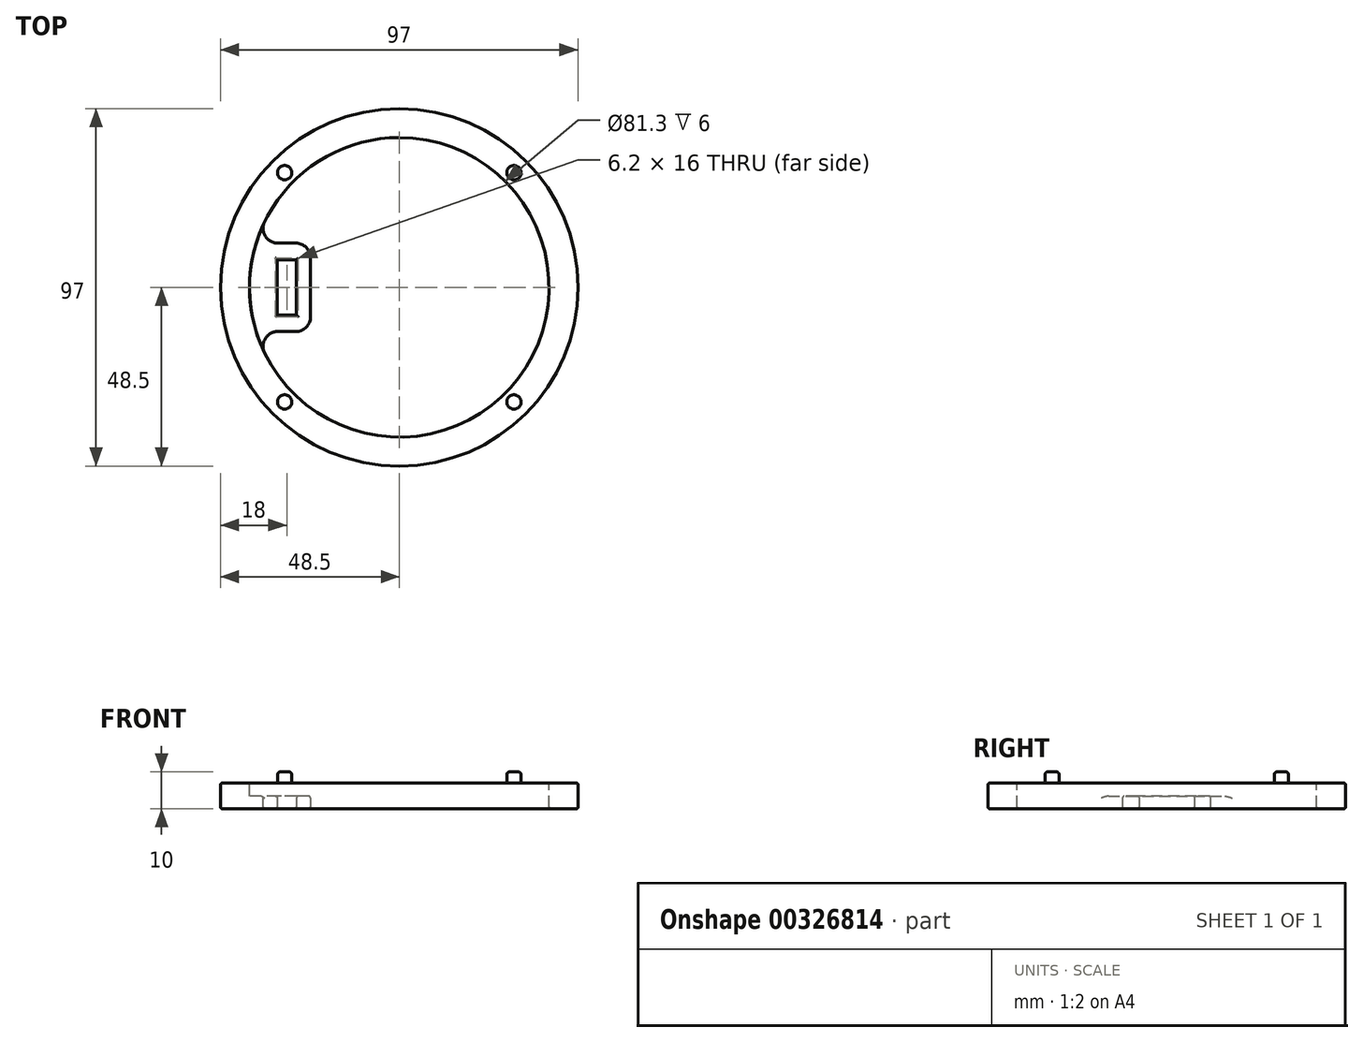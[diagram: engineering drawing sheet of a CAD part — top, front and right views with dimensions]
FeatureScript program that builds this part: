
annotation { "Feature Type Name" : "Feature", "Feature Type Description" : "" }
export const myFeature = defineFeature(function(context is Context, id is Id, definition is map)
    precondition{}
    {
        {
            var Q0;
            Q0=qCreatedBy(makeId("Top.planeOp"),FACE);
            var sketch = newSketch(context, id + "F0", { "sketchPlane" : qUnion([Q0])});
            skCircle(sketch, "E0", {"center": v(0, 0) * mm, "radius": 40.65 * mm});
            skCircle(sketch, "E1", {"center": v(0, 0) * mm, "radius": 48.5 * mm});
            skCircle(sketch, "E2", {"center": v(0, 0) * mm, "radius": 44 * mm, "construction": true});
            skCircle(sketch, "E3", {"center": v(-31.11, 31.11) * mm, "radius": 1.95 * mm});
            skCircle(sketch, "E4", {"center": v(31.11, -31.11) * mm, "radius": 1.95 * mm});
            skCircle(sketch, "E5", {"center": v(31.11, 31.11) * mm, "radius": 1.95 * mm});
            skCircle(sketch, "E6", {"center": v(-31.11, -31.11) * mm, "radius": 1.95 * mm});
            skLineSegment(sketch, "E7.0", {"start": v(-31.11, -31.11) * mm, "end": v(31.11, 31.11) * mm, "construction": true});
            skLineSegment(sketch, "E8.0", {"start": v(31.11, -31.11) * mm, "end": v(-31.11, 31.11) * mm, "construction": true});
            skSolve(sketch);
        }
        {
            var Q0;
            Q0=makeQuery(id+"F0.imprint","IMPRINT",FACE,{"disambiguationData":[TD([[makeQuery(id+"F0.imprint","IMPRINT",EDGE,{"derivedFrom":sQuery(id+"F0.wireOp",EDGE,"E0")}),-1.0]])]});
            var Q1;
            Q1=makeQuery(id+"F0.imprint","IMPRINT",FACE,{"disambiguationData":[TD([[makeQuery(id+"F0.imprint","IMPRINT",EDGE,{"derivedFrom":sQuery(id+"F0.wireOp",EDGE,"E3")}),1.0]])]});
            var Q2;
            Q2=makeQuery(id+"F0.imprint","IMPRINT",FACE,{"disambiguationData":[TD([[makeQuery(id+"F0.imprint","IMPRINT",EDGE,{"derivedFrom":sQuery(id+"F0.wireOp",EDGE,"E5")}),1.0]])]});
            var Q3;
            Q3=makeQuery(id+"F0.imprint","IMPRINT",FACE,{"disambiguationData":[TD([[makeQuery(id+"F0.imprint","IMPRINT",EDGE,{"derivedFrom":sQuery(id+"F0.wireOp",EDGE,"E4")}),1.0]])]});
            var Q4;
            Q4=makeQuery(id+"F0.imprint","IMPRINT",FACE,{"disambiguationData":[TD([[makeQuery(id+"F0.imprint","IMPRINT",EDGE,{"derivedFrom":sQuery(id+"F0.wireOp",EDGE,"E6")}),1.0]])]});
            extrude(context, id + "F1", {"entities" : qUnion([Q0, Q1, Q2, Q3, Q4]), "depth" : 7 * mm});
        }
        {
            var Q0;
            Q0=makeQuery(id+"F0.imprint","IMPRINT",FACE,{"disambiguationData":[TD([[makeQuery(id+"F0.imprint","IMPRINT",EDGE,{"derivedFrom":sQuery(id+"F0.wireOp",EDGE,"E5")}),1.0]])]});
            var Q1;
            Q1=makeQuery(id+"F0.imprint","IMPRINT",FACE,{"disambiguationData":[TD([[makeQuery(id+"F0.imprint","IMPRINT",EDGE,{"derivedFrom":sQuery(id+"F0.wireOp",EDGE,"E3")}),1.0]])]});
            var Q2;
            Q2=makeQuery(id+"F0.imprint","IMPRINT",FACE,{"disambiguationData":[TD([[makeQuery(id+"F0.imprint","IMPRINT",EDGE,{"derivedFrom":sQuery(id+"F0.wireOp",EDGE,"E6")}),1.0]])]});
            var Q3;
            Q3=makeQuery(id+"F0.imprint","IMPRINT",FACE,{"disambiguationData":[TD([[makeQuery(id+"F0.imprint","IMPRINT",EDGE,{"derivedFrom":sQuery(id+"F0.wireOp",EDGE,"E4")}),1.0]])]});
            extrude(context, id + "F2", {"entities" : qUnion([Q0, Q1, Q2, Q3]), "operationType" : NewBodyOperationType.ADD, "oppositeDirection" : true, "depth" : 3 * mm});
        }
        {
            var Q0;
            Q0=makeQuery(id+"F2.opExtrude","CAP_EDGE",EDGE,{"disambiguationData":[OSD([sQuery(id+"F0.wireOp",EDGE,"E5")])],"isStart":false});
            var Q1;
            Q1=makeQuery(id+"F2.opExtrude","CAP_EDGE",EDGE,{"disambiguationData":[OSD([sQuery(id+"F0.wireOp",EDGE,"E3")])],"isStart":false});
            var Q2;
            Q2=makeQuery(id+"F2.opExtrude","CAP_EDGE",EDGE,{"disambiguationData":[OSD([sQuery(id+"F0.wireOp",EDGE,"E6")])],"isStart":false});
            var Q3;
            Q3=makeQuery(id+"F2.opExtrude","CAP_EDGE",EDGE,{"disambiguationData":[OSD([sQuery(id+"F0.wireOp",EDGE,"E4")])],"isStart":false});
            fillet(context, id + "F3", {"entities" : qUnion([Q0, Q1, Q2, Q3]), "radius" : .8 * mm, "tangentPropagation" : true, "allowEdgeOverflow" : false});
        }
        {
            var Q0;
            Q0=makeQuery(id+"F1.opExtrude","CAP_FACE",FACE,{"disambiguationData":[OSD([sQuery(id+"F0.wireOp",EDGE,"E0"),sQuery(id+"F0.wireOp",EDGE,"E1")])],"isStart":false});
            var sketch = newSketch(context, id + "F4", { "sketchPlane" : qUnion([Q0])});
            skLineSegment(sketch, "E9.bottom", {"start": v(7.5, -27.9) * mm, "end": v(-7.5, -27.9) * mm});
            skLineSegment(sketch, "E9.top", {"start": v(7.5, -33.1) * mm, "end": v(-7.5, -33.1) * mm});
            skLineSegment(sketch, "E9.left", {"start": v(7.5, -27.9) * mm, "end": v(7.5, -33.1) * mm});
            skLineSegment(sketch, "E9.right", {"start": v(-7.5, -27.9) * mm, "end": v(-7.5, -33.1) * mm});
            skPoint(sketch, "E9.middle", {"position": v(0, -30.5) * mm});
            skLineSegment(sketch, "E10.bottom", {"start": v(12, -24.1) * mm, "end": v(-12, -24.1) * mm});
            skLineSegment(sketch, "E10.top", {"start": v(12, -42.1) * mm, "end": v(-12, -42.1) * mm});
            skLineSegment(sketch, "E10.left", {"start": v(12, -24.1) * mm, "end": v(12, -42.1) * mm});
            skLineSegment(sketch, "E10.right", {"start": v(-12, -24.1) * mm, "end": v(-12, -42.1) * mm});
            skPoint(sketch, "E10.middle", {"position": v(0, -33.1) * mm});
            skSolve(sketch);
        }
        {
            var Q0;
            Q0=makeQuery(id+"F4.imprint","IMPRINT",FACE,{"disambiguationData":[TD([[makeQuery(id+"F4.imprint","IMPRINT",EDGE,{"derivedFrom":sQuery(id+"F4.wireOp",EDGE,"E9.bottom")}),-1.0]])]});
            var Q1;
            {var subQ0=sQuery(id+"F4.wireOp",EDGE,"E10.top");Q1=makeQuery(id+"F4.imprint","IMPRINT",FACE,{"disambiguationData":[TD([[makeQuery(id+"F4.imprint","IMPRINT",EDGE,{"derivedFrom":subQ0}),-1.0]])]});}
            extrude(context, id + "F5", {"entities" : qUnion([Q0, Q1]), "operationType" : NewBodyOperationType.ADD, "oppositeDirection" : true, "depth" : 3.4 * mm});
        }
        {
            var Q0;
            Q0=makeQuery(id+"F5.opExtrude","SWEPT_EDGE",EDGE,{"disambiguationData":[OSD([sQuery(id+"F4.wireOp",EDGE,"E10.bottom"),sQuery(id+"F4.wireOp",EDGE,"E10.right")])]});
            var Q1;
            Q1=makeQuery(id+"F5.opExtrude","SWEPT_EDGE",EDGE,{"disambiguationData":[OSD([sQuery(id+"F4.wireOp",EDGE,"E10.bottom"),sQuery(id+"F4.wireOp",EDGE,"E10.left")])]});
            var Q2;
            Q2=makeQuery(id+"F5.boolean.opBoolean","INTERSECT",EDGE,{"derivedFrom":[makeQuery(id+"F1.opExtrude","SWEPT_FACE",FACE,{"disambiguationData":[OSD([sQuery(id+"F0.wireOp",EDGE,"E0")])]}),makeQuery(id+"F5.opExtrude","SWEPT_FACE",FACE,{"disambiguationData":[OSD([sQuery(id+"F4.wireOp",EDGE,"E10.left")])]})]});
            var Q3;
            Q3=makeQuery(id+"F5.boolean.opBoolean","INTERSECT",EDGE,{"derivedFrom":[makeQuery(id+"F1.opExtrude","SWEPT_FACE",FACE,{"disambiguationData":[OSD([sQuery(id+"F0.wireOp",EDGE,"E0")])]}),makeQuery(id+"F5.opExtrude","SWEPT_FACE",FACE,{"disambiguationData":[OSD([sQuery(id+"F4.wireOp",EDGE,"E10.right")])]})]});
            fillet(context, id + "F6", {"entities" : qUnion([Q0, Q1, Q2, Q3]), "radius" : 4 * mm, "tangentPropagation" : true, "allowEdgeOverflow" : false});
        }
        {
            var Q0;
            Q0=makeQuery(id+"F5.boolean.opBoolean","MERGE",FACE,{"derivedFrom":[makeQuery(id+"F1.opExtrude","CAP_FACE",FACE,{"disambiguationData":[OSD([sQuery(id+"F0.wireOp",EDGE,"E0"),sQuery(id+"F0.wireOp",EDGE,"E1")])],"isStart":false}),makeQuery(id+"F5.opExtrude","CAP_FACE",FACE,{"disambiguationData":[OSD([sQuery(id+"F4.wireOp",EDGE,"E9.bottom"),sQuery(id+"F4.wireOp",EDGE,"E9.top"),sQuery(id+"F4.wireOp",EDGE,"E9.left"),sQuery(id+"F4.wireOp",EDGE,"E9.right"),sQuery(id+"F4.wireOp",EDGE,"E10.bottom"),sQuery(id+"F4.wireOp",EDGE,"E10.top"),sQuery(id+"F4.wireOp",EDGE,"E10.left"),sQuery(id+"F4.wireOp",EDGE,"E10.right")])],"isStart":true})]});
            fillet(context, id + "F7", {"entities" : qUnion([Q0]), "radius" : .5 * mm, "tangentPropagation" : true, "allowEdgeOverflow" : false});
        }
        {
            var Q0;
            Q0=makeQuery(id+"F1.opExtrude","CAP_EDGE",EDGE,{"disambiguationData":[OSD([sQuery(id+"F0.wireOp",EDGE,"E1")])],"isStart":true});
            var Q1;
            Q1=makeQuery(id+"F1.opExtrude","CAP_EDGE",EDGE,{"disambiguationData":[OSD([sQuery(id+"F0.wireOp",EDGE,"E0")])],"isStart":true});
            var Q2;
            Q2=makeQuery(id+"F5.opExtrude","CAP_EDGE",EDGE,{"disambiguationData":[OSD([sQuery(id+"F4.wireOp",EDGE,"E9.right")])],"isStart":false});
            var Q3;
            Q3=makeQuery(id+"F5.opExtrude","CAP_EDGE",EDGE,{"disambiguationData":[OSD([sQuery(id+"F4.wireOp",EDGE,"E9.bottom")])],"isStart":false});
            var Q4;
            Q4=makeQuery(id+"F5.opExtrude","CAP_EDGE",EDGE,{"disambiguationData":[OSD([sQuery(id+"F4.wireOp",EDGE,"E9.left")])],"isStart":false});
            var Q5;
            Q5=makeQuery(id+"F5.opExtrude","CAP_EDGE",EDGE,{"disambiguationData":[OSD([sQuery(id+"F4.wireOp",EDGE,"E9.top")])],"isStart":false});
            var Q6;
            {var subQ0=sQuery(id+"F4.wireOp",EDGE,"E10.right");Q6=makeQuery(id+"F6.opFillet","BLEND_EDGE",EDGE,{"blendedFrom":[makeQuery(id+"F5.boolean.opBoolean","INTERSECT",EDGE,{"derivedFrom":[makeQuery(id+"F1.opExtrude","SWEPT_FACE",FACE,{"disambiguationData":[OSD([sQuery(id+"F0.wireOp",EDGE,"E0")])]}),makeQuery(id+"F5.opExtrude","SWEPT_FACE",FACE,{"disambiguationData":[OSD([subQ0])]})]}),makeQuery(id+"F5.opExtrude","CAP_FACE",FACE,{"disambiguationData":[OSD([sQuery(id+"F4.wireOp",EDGE,"E9.bottom"),sQuery(id+"F4.wireOp",EDGE,"E9.top"),sQuery(id+"F4.wireOp",EDGE,"E9.left"),sQuery(id+"F4.wireOp",EDGE,"E9.right"),sQuery(id+"F4.wireOp",EDGE,"E10.bottom"),sQuery(id+"F4.wireOp",EDGE,"E10.top"),sQuery(id+"F4.wireOp",EDGE,"E10.left"),subQ0])],"isStart":false})],"blendedInto":[makeQuery(id+"F5.opExtrude","CAP_FACE",FACE,{"disambiguationData":[OSD([sQuery(id+"F4.wireOp",EDGE,"E9.bottom"),sQuery(id+"F4.wireOp",EDGE,"E9.top"),sQuery(id+"F4.wireOp",EDGE,"E9.left"),sQuery(id+"F4.wireOp",EDGE,"E9.right"),sQuery(id+"F4.wireOp",EDGE,"E10.bottom"),sQuery(id+"F4.wireOp",EDGE,"E10.top"),sQuery(id+"F4.wireOp",EDGE,"E10.left"),subQ0])],"isStart":false})]});}
            var Q7;
            Q7=makeQuery(id+"F5.opExtrude","CAP_EDGE",EDGE,{"disambiguationData":[OSD([sQuery(id+"F4.wireOp",EDGE,"E10.right")])],"isStart":false});
            fillet(context, id + "F8", {"entities" : qUnion([Q0, Q1, Q2, Q3, Q4, Q5, Q6, Q7]), "radius" : .5 * mm, "tangentPropagation" : true, "allowEdgeOverflow" : false});
        }
        {
            var Q0;
            Q0=makeQuery(id+"F1.opExtrude","SWEPT_BODY",BODY,{"disambiguationData":[OSD([sQuery(id+"F0.wireOp",EDGE,"E0"),sQuery(id+"F0.wireOp",EDGE,"E1")])]});
            var Q1;
            Q1=sQuery(id+"F0.wireOp",EDGE,"E7.0");
            transform(context, id + "F9", {"entities" : qUnion([Q0]), "transformType" : TransformType.ROTATION, "transformAxis" : qUnion([Q1]), "angle" : 180 * degree, "makeCopy" : false});
        }
    });
